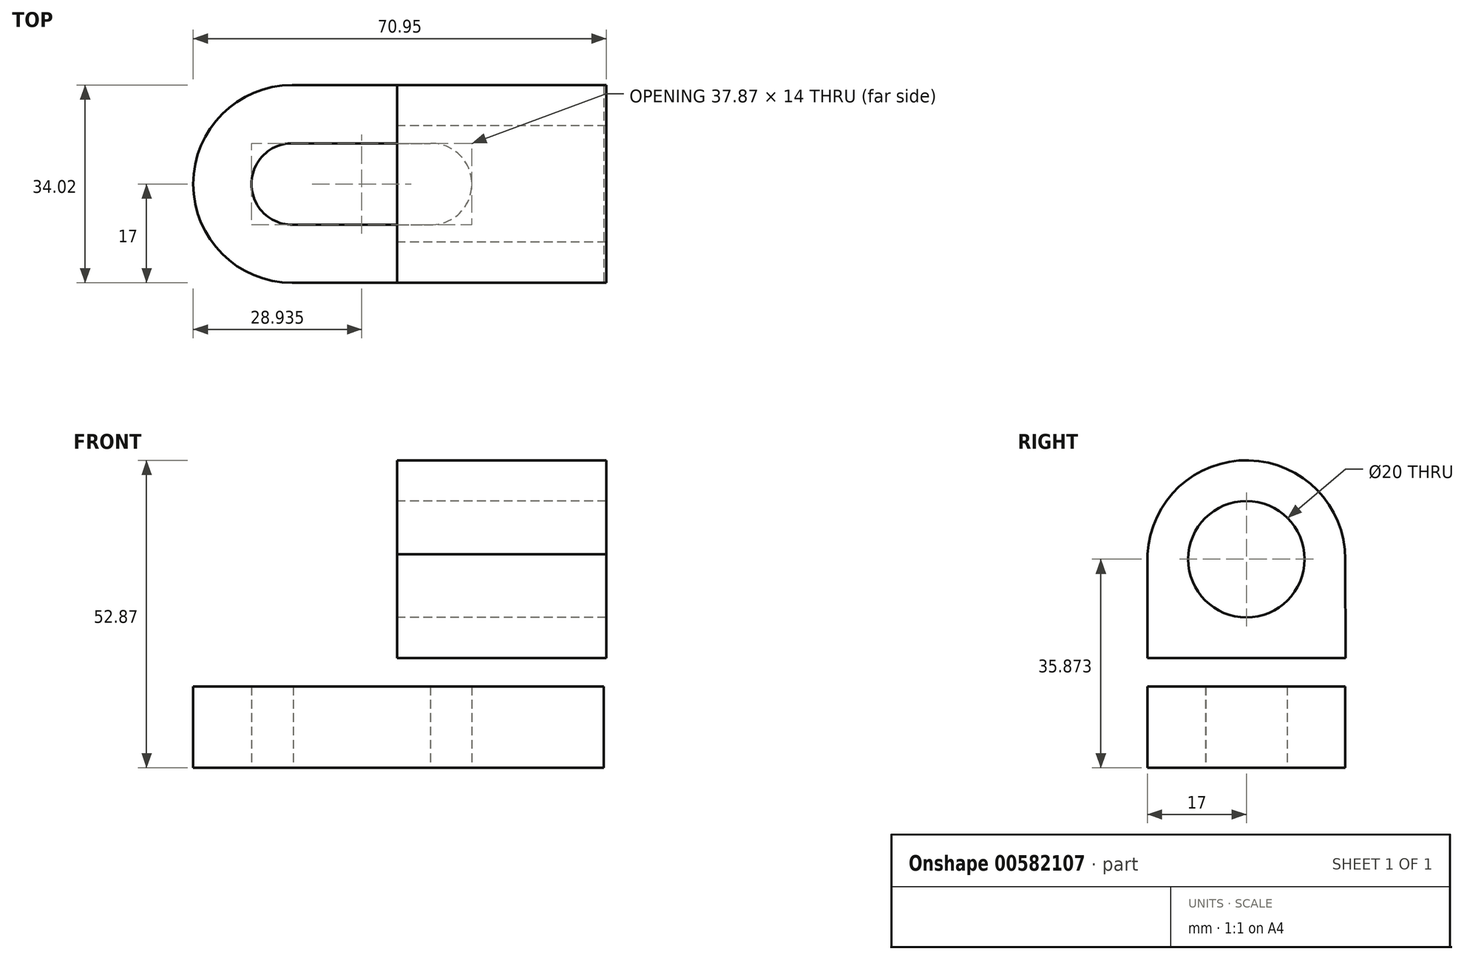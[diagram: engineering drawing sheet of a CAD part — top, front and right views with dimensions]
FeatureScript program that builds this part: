
annotation { "Feature Type Name" : "Feature", "Feature Type Description" : "" }
export const myFeature = defineFeature(function(context is Context, id is Id, definition is map)
    precondition{}
    {
        {
            var Q0;
            Q0=qCreatedBy(makeId("Top.planeOp"),FACE);
            var sketch = newSketch(context, id + "F0", { "sketchPlane" : qUnion([Q0])});
            skLineSegment(sketch, "E0.bottom", {"start": v(-18.05, 17) * mm, "end": v(35.5, 17) * mm});
            skLineSegment(sketch, "E0.top", {"start": v(-18.05, -17) * mm, "end": v(35.5, -17) * mm});
            skLineSegment(sketch, "E0.right", {"start": v(35.5, 17) * mm, "end": v(35.5, -17) * mm});
            skPoint(sketch, "E0.middle", {"position": v(0, 0) * mm});
            skArc(sketch, "E1", {"start": v(-18.05, 17) * mm, "mid": v(-35.05, 0) * mm, "end": v(-18.05, -17) * mm});
            skPoint(sketch, "E1.centerSnap0", {"position": v(-35.5, 0) * mm});
            skPoint(sketch, "E2.orphan", {"position": v(-35.5, 17) * mm});
            skPoint(sketch, "E3.orphan", {"position": v(-35.5, -17) * mm});
            skArc(sketch, "E4", {"start": v(-17.9, 7) * mm, "mid": v(-25.05, 0) * mm, "end": v(-17.9, -7) * mm});
            skLineSegment(sketch, "E5.bottom", {"start": v(-17.9, 7) * mm, "end": v(5.95, 7) * mm});
            skLineSegment(sketch, "E5.top", {"start": v(-17.9, -7) * mm, "end": v(5.95, -7) * mm});
            skLineSegment(sketch, "E5.left", {"start": v(-17.9, -7) * mm, "end": v(-17.9, -7) * mm});
            skPoint(sketch, "E6.trimOffspring.start.orphan", {"position": v(5.95, 0) * mm});
            skArc(sketch, "E7", {"start": v(5.68, -7) * mm, "mid": v(12.82, 0) * mm, "end": v(5.68, 7) * mm});
            skPoint(sketch, "E7.third.point", {"position": v(12.82, 0) * mm});
            skSolve(sketch);
        }
        {
            var Q0;
            Q0=makeQuery(id+"F0.imprint","IMPRINT",FACE,{"disambiguationData":[TD([[makeQuery(id+"F0.imprint","IMPRINT",EDGE,{"derivedFrom":sQuery(id+"F0.wireOp",EDGE,"E0.bottom")}),-1.0]])]});
            extrude(context, id + "F1", {"entities" : qUnion([Q0]), "depth" : 14 * mm, "offsetDistance" : 25 * mm});
        }
        {
            var Q0;
            Q0=qCreatedBy(makeId("Right.planeOp"),FACE);
            var sketch = newSketch(context, id + "F2", { "sketchPlane" : qUnion([Q0])});
            skLineSegment(sketch, "E8.bottom", {"start": v(-16.98, 18.87) * mm, "end": v(17.02, 18.87) * mm});
            skLineSegment(sketch, "E8.left", {"start": v(-16.98, 18.87) * mm, "end": v(-16.98, 36.7) * mm});
            skPoint(sketch, "E9.first.point", {"position": v(0, 52.87) * mm});
            skPoint(sketch, "E9.second.point", {"position": v(0, 18.87) * mm});
            skPoint(sketch, "E9.third.point", {"position": v(4.09, 21.47) * mm});
            skArc(sketch, "E10", {"start": v(17, 35.87) * mm, "mid": v(-0.42, 52.87) * mm, "end": v(-16.98, 35.04) * mm});
            skPoint(sketch, "E10.centerSnap0", {"position": v(-16.98, 35.87) * mm});
            skPoint(sketch, "E11.orphan", {"position": v(-16.98, 52.87) * mm});
            skLineSegment(sketch, "E12", {"start": v(17, 35.87) * mm, "end": v(17.02, 18.87) * mm});
            skCircle(sketch, "E13", {"center": v(0, 35.87) * mm, "radius": 10 * mm});
            skSolve(sketch);
        }
        {
            var Q0;
            {var subQ5=sQuery(id+"F2.wireOp",EDGE,"E8.bottom");Q0=makeQuery(id+"F2.imprint","IMPRINT",FACE,{"disambiguationData":[TD([[makeQuery(id+"F2.imprint","IMPRINT",EDGE,{"derivedFrom":subQ5}),1.0]])]});}
            extrude(context, id + "F3", {"entities" : qUnion([Q0]), "depth" : 35.9 * mm, "offsetDistance" : 25 * mm});
        }
    });
